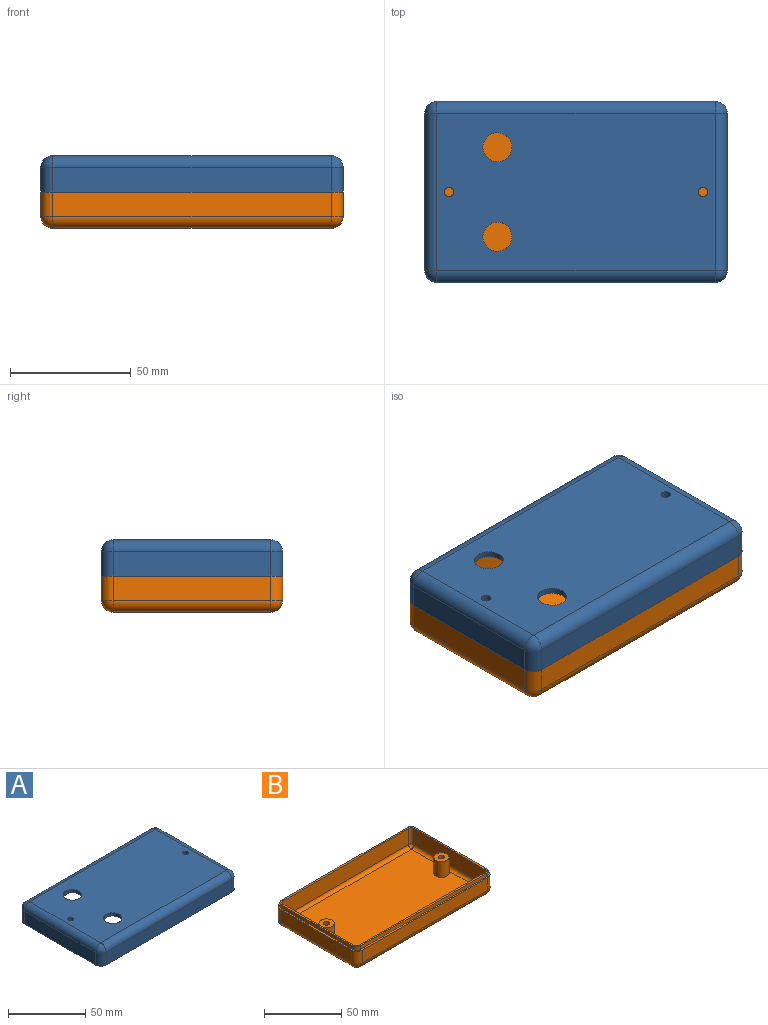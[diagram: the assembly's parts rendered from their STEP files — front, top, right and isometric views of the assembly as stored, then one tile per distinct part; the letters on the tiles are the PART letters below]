
ASSEMBLY  parts=2 mates=1
PART A: 52 faces, bbox 125x75x15 mm
  f0: plane 115x65mm, normal (0,0,-1), area 7091.7mm2, adj f25,f26,f31,f32,f47,f49,f50,f51
  f1: plane 125x75mm, normal (0,0,-1), area 484.4mm2, adj f2,f3,f4,f5,f7,f11,f12,f18
  f2: plane 65x10mm, normal (1,0,0), area 650mm2, adj f1,f12,f15,f18
  f3: plane 115x10mm, normal (0,1,0), area 1150mm2, adj f1,f11,f16,f18
  f4: plane 65x10mm, normal (-1,0,0), area 650mm2, adj f1,f7,f10,f11
  f5: plane 115x10mm, normal (0,-1,0), area 1150mm2, adj f1,f7,f9,f12
  f6: plane 115x65mm, normal (0,0,1), area 7223.7mm2, adj f9,f10,f15,f16,f35,f36,f50,f51
  f7: cylinder r=5mm len=10mm, axis (0,0,1), area 78.5mm2, adj f1,f4,f5,f8
  f8: sphere r=5mm, area 39.3mm2, adj f7,f9,f10
  f9: cylinder r=5mm len=115mm, axis (-1,0,0), area 903.2mm2, adj f5,f6,f8,f13
  f10: cylinder r=5mm len=65mm, axis (0,1,0), area 510.5mm2, adj f4,f6,f8,f14
  f11: cylinder r=5mm len=10mm, axis (0,0,-1), area 78.5mm2, adj f1,f3,f4,f14
  f12: cylinder r=5mm len=10mm, axis (0,0,-1), area 78.5mm2, adj f1,f2,f5,f13
  f13: sphere r=5mm, area 39.3mm2, adj f9,f12,f15
  f14: sphere r=5mm, area 39.3mm2, adj f10,f11,f16
  f15: cylinder r=5mm len=65mm, axis (0,-1,0), area 510.5mm2, adj f2,f6,f13,f17
  f16: cylinder r=5mm len=115mm, axis (1,0,0), area 903.2mm2, adj f3,f6,f14,f17
  f17: sphere r=5mm, area 39.3mm2, adj f15,f16,f18
  f18: cylinder r=5mm len=10mm, axis (0,0,1), area 78.5mm2, adj f1,f2,f3,f17
  f19: plane 65x7.25mm, normal (-1,0,0), area 471.3mm2, adj f28,f31,f34,f44
  f20: plane 115x7.25mm, normal (0,-1,0), area 833.8mm2, adj f27,f32,f34,f44
  f21: plane 65x7.25mm, normal (1,0,0), area 471.3mm2, adj f23,f26,f27,f44
  f22: plane 115x7.25mm, normal (0,1,0), area 833.8mm2, adj f23,f25,f28,f44
  f23: cylinder r=2.5mm len=7.25mm, axis (0,0,1), area 28.5mm2, adj f21,f22,f24,f44
  f24: sphere r=2.5mm, area 9.8mm2, adj f23,f25,f26
  f25: cylinder r=2.5mm len=115mm, axis (-1,0,0), area 451.6mm2, adj f0,f22,f24,f29
  f26: cylinder r=2.5mm len=65mm, axis (0,1,0), area 255.3mm2, adj f0,f21,f24,f30
  f27: cylinder r=2.5mm len=7.25mm, axis (0,0,-1), area 28.5mm2, adj f20,f21,f30,f44
  f28: cylinder r=2.5mm len=7.25mm, axis (0,0,-1), area 28.5mm2, adj f19,f22,f29,f44
  f29: sphere r=2.5mm, area 9.8mm2, adj f25,f28,f31
  f30: sphere r=2.5mm, area 9.8mm2, adj f26,f27,f32
  f31: cylinder r=2.5mm len=65mm, axis (0,-1,0), area 255.3mm2, adj f0,f19,f29,f33
  f32: cylinder r=2.5mm len=115mm, axis (1,0,0), area 451.6mm2, adj f0,f20,f30,f33
  f33: sphere r=2.5mm, area 9.8mm2, adj f31,f32,f34
  f34: cylinder r=2.5mm len=7.25mm, axis (0,0,1), area 28.5mm2, adj f19,f20,f33,f44
  f35: cylinder r=2mm len=15mm, axis (0,0,-1), area 188.5mm2, adj f6,f48
  f36: cylinder r=2mm len=15mm, axis (0,0,-1), area 188.5mm2, adj f6,f46
  f37: cylinder r=3.75mm len=3.75mm, axis (0,0,-1), area 16.2mm2, adj f1,f38,f44,f45
  f38: plane 65x2.75mm, normal (1,0,0), area 178.8mm2, adj f1,f37,f39,f44
  f39: cylinder r=3.75mm len=3.75mm, axis (0,0,-1), area 16.2mm2, adj f1,f38,f40,f44
  f40: plane 115x2.75mm, normal (0,1,0), area 316.3mm2, adj f1,f39,f41,f44
  f41: cylinder r=3.75mm len=3.75mm, axis (0,0,-1), area 16.2mm2, adj f1,f40,f42,f44
  f42: plane 65x2.75mm, normal (-1,0,0), area 178.8mm2, adj f1,f41,f43,f44
  f43: cylinder r=3.75mm len=3.75mm, axis (0,0,-1), area 16.2mm2, adj f1,f42,f44,f45
  f44: plane 122.5x72.5mm, normal (0,0,-1), area 474.5mm2, adj f19,f20,f21,f22,f23,f27,f28,f34
  f45: plane 115x2.75mm, normal (0,-1,0), area 316.3mm2, adj f1,f37,f43,f44
  f46: plane 10x10mm, normal (0,0,-1), area 66mm2, adj f36,f47
  f47: cylinder r=5mm len=12.5mm, axis (0,0,-1), area 392.7mm2, adj f0,f46
  f48: plane 10x10mm, normal (0,0,-1), area 66mm2, adj f35,f49
  f49: cylinder r=5mm len=12.5mm, axis (0,0,-1), area 392.7mm2, adj f0,f48
  f50: cylinder r=6mm len=12mm, axis (0,0,1), area 94.2mm2, adj f0,f6
  f51: cylinder r=6mm len=12mm, axis (0,0,1), area 94.2mm2, adj f0,f6
PART B: 52 faces, bbox 125x75x17.8 mm
  f0: plane 115x65mm, normal (0,0,1), area 7317.9mm2, adj f1,f2,f3,f4,f18,f21
  f1: cylinder r=2.5mm len=65mm, axis (0,1,0), area 255.3mm2, adj f0,f7,f8,f16
  f2: cylinder r=2.5mm len=115mm, axis (-1,0,0), area 451.6mm2, adj f0,f6,f8,f15
  f3: cylinder r=2.5mm len=65mm, axis (0,-1,0), area 255.3mm2, adj f0,f5,f6,f13
  f4: cylinder r=2.5mm len=115mm, axis (1,0,0), area 451.6mm2, adj f0,f5,f7,f11
  f5: sphere r=2.5mm, area 9.8mm2, adj f3,f4,f9
  f6: sphere r=2.5mm, area 9.8mm2, adj f2,f3,f12
  f7: sphere r=2.5mm, area 9.8mm2, adj f1,f4,f10
  f8: sphere r=2.5mm, area 9.8mm2, adj f1,f2,f14
  f9: cylinder r=2.5mm len=12.75mm, axis (0,0,1), area 50.1mm2, adj f5,f11,f13,f32
  f10: cylinder r=2.5mm len=12.75mm, axis (0,0,-1), area 50.1mm2, adj f7,f11,f16,f32
  f11: plane 115x12.75mm, normal (0,1,0), area 1466.2mm2, adj f4,f9,f10,f32
  f12: cylinder r=2.5mm len=12.75mm, axis (0,0,-1), area 50.1mm2, adj f6,f13,f15,f32
  f13: plane 65x12.75mm, normal (1,0,0), area 828.8mm2, adj f3,f9,f12,f32
  f14: cylinder r=2.5mm len=12.75mm, axis (0,0,1), area 50.1mm2, adj f8,f15,f16,f32
  f15: plane 115x12.75mm, normal (0,-1,0), area 1466.2mm2, adj f2,f12,f14,f32
  f16: plane 65x12.75mm, normal (-1,0,0), area 828.8mm2, adj f1,f10,f14,f32
  f17: cylinder r=2mm len=12.5mm, axis (0,0,1), area 157.1mm2, adj f19,f20
  f18: cylinder r=5mm len=12.5mm, axis (0,0,1), area 392.7mm2, adj f0,f19
  f19: plane 10x10mm, normal (0,0,1), area 66mm2, adj f17,f18
  f20: plane 4x4mm, normal (0,0,1), area 12.6mm2, adj f17
  f21: cylinder r=5mm len=12.5mm, axis (0,0,1), area 392.7mm2, adj f0,f23
  f22: cylinder r=2mm len=12.5mm, axis (0,0,1), area 157.1mm2, adj f23,f24
  f23: plane 10x10mm, normal (0,0,1), area 66mm2, adj f21,f22
  f24: plane 4x4mm, normal (0,0,1), area 12.6mm2, adj f22
  f25: cylinder r=3.75mm len=3.75mm, axis (0,0,-1), area 16.2mm2, adj f26,f32,f33,f51
  f26: plane 65x2.75mm, normal (-1,0,0), area 178.8mm2, adj f25,f27,f32,f51
  f27: cylinder r=3.75mm len=3.75mm, axis (0,0,-1), area 16.2mm2, adj f26,f28,f32,f51
  f28: plane 115x2.75mm, normal (0,-1,0), area 316.3mm2, adj f27,f29,f32,f51
  f29: cylinder r=3.75mm len=3.75mm, axis (0,0,-1), area 16.2mm2, adj f28,f30,f32,f51
  f30: plane 65x2.75mm, normal (1,0,0), area 178.8mm2, adj f29,f31,f32,f51
  f31: cylinder r=3.75mm len=3.75mm, axis (0,0,-1), area 16.2mm2, adj f30,f32,f33,f51
  f32: plane 122.5x72.5mm, normal (0,0,1), area 474.5mm2, adj f9,f10,f11,f12,f13,f14,f15,f16
  f33: plane 115x2.75mm, normal (0,1,0), area 316.3mm2, adj f25,f31,f32,f51
  f34: plane 115x65mm, normal (0,0,-1), area 7475mm2, adj f35,f37,f39,f41
  f35: cylinder r=5mm len=65mm, axis (0,-1,0), area 510.5mm2, adj f34,f36,f42,f43
  f36: sphere r=5mm, area 39.3mm2, adj f35,f37,f44
  f37: cylinder r=5mm len=115mm, axis (-1,0,0), area 903.2mm2, adj f34,f36,f38,f45
  f38: sphere r=5mm, area 39.3mm2, adj f37,f39,f46
  f39: cylinder r=5mm len=65mm, axis (0,1,0), area 510.5mm2, adj f34,f38,f40,f47
  f40: sphere r=5mm, area 39.3mm2, adj f39,f41,f48
  f41: cylinder r=5mm len=115mm, axis (1,0,0), area 903.2mm2, adj f34,f40,f42,f49
  f42: sphere r=5mm, area 39.3mm2, adj f35,f41,f50
  f43: plane 65x10mm, normal (-1,0,0), area 650mm2, adj f35,f44,f50,f51
  f44: cylinder r=5mm len=10mm, axis (0,0,-1), area 78.5mm2, adj f36,f43,f45,f51
  f45: plane 115x10mm, normal (0,1,0), area 1150mm2, adj f37,f44,f46,f51
  f46: cylinder r=5mm len=10mm, axis (0,0,1), area 78.5mm2, adj f38,f45,f47,f51
  f47: plane 65x10mm, normal (1,0,0), area 650mm2, adj f39,f46,f48,f51
  f48: cylinder r=5mm len=10mm, axis (0,0,-1), area 78.5mm2, adj f40,f47,f49,f51
  f49: plane 115x10mm, normal (0,-1,0), area 1150mm2, adj f41,f48,f50,f51
  f50: cylinder r=5mm len=10mm, axis (0,0,1), area 78.5mm2, adj f42,f43,f49,f51
  f51: plane 125x75mm, normal (0,0,1), area 484.4mm2, adj f25,f26,f27,f28,f29,f30,f31,f33
PLACE A at identity
PLACE B at identity fixed
MATE slider B.f17 <-> A.f36  axis (0,0,1) through (-52.5,0,0)mm
